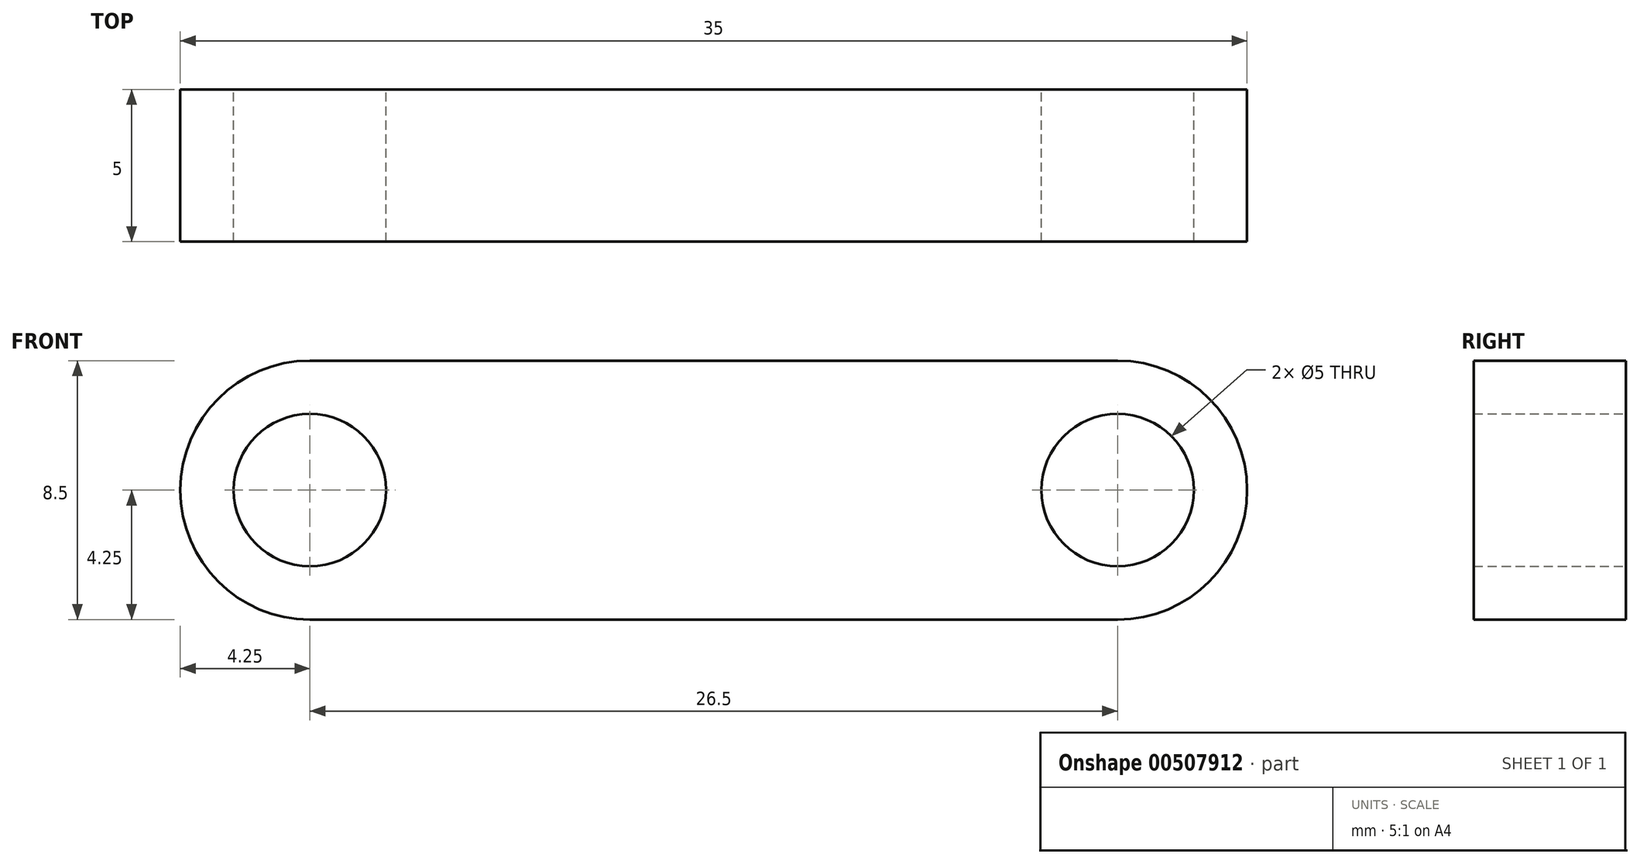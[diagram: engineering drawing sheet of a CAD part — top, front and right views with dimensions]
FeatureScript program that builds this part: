
annotation { "Feature Type Name" : "Feature", "Feature Type Description" : "" }
export const myFeature = defineFeature(function(context is Context, id is Id, definition is map)
    precondition{}
    {
        {
            var Q0;
            Q0=qCreatedBy(makeId("Front.planeOp"),FACE);
            var sketch = newSketch(context, id + "F0", { "sketchPlane" : qUnion([Q0])});
            skCircle(sketch, "E0", {"center": v(0, 0) * mm, "radius": 2.5 * mm});
            skLineSegment(sketch, "E1", {"start": v(0, 0) * mm, "end": v(26.5, 0) * mm, "construction": true});
            skCircle(sketch, "E2", {"center": v(26.5, 0) * mm, "radius": 2.5 * mm});
            skCircle(sketch, "E3", {"center": v(0, 0) * mm, "radius": 4.25 * mm});
            skCircle(sketch, "E4", {"center": v(26.5, 0) * mm, "radius": 4.25 * mm});
            skLineSegment(sketch, "E5", {"start": v(0, -4.25) * mm, "end": v(26.5, -4.25) * mm});
            skLineSegment(sketch, "E6", {"start": v(0, 4.25) * mm, "end": v(26.5, 4.25) * mm});
            skSolve(sketch);
        }
        {
            var Q0;
            Q0=makeQuery(id+"F0.imprint","IMPRINT",FACE,{"disambiguationData":[TD([[makeQuery(id+"F0.imprint","IMPRINT",EDGE,{"derivedFrom":sQuery(id+"F0.wireOp",EDGE,"E0")}),-1.0]])]});
            var Q1;
            Q1=makeQuery(id+"F0.imprint","IMPRINT",FACE,{"disambiguationData":[TD([[makeQuery(id+"F0.imprint","IMPRINT",EDGE,{"derivedFrom":sQuery(id+"F0.wireOp",EDGE,"E2")}),-1.0]])]});
            var Q2;
            {var subQ0=sQuery(id+"F0.wireOp",EDGE,"E5");Q2=makeQuery(id+"F0.imprint","IMPRINT",FACE,{"disambiguationData":[TD([[makeQuery(id+"F0.imprint","IMPRINT",EDGE,{"derivedFrom":subQ0}),1.0]])]});}
            var Q3;
            Q3=sQuery(id+"F0.wireOp",EDGE,"E0");
            var Q4;
            Q4=sQuery(id+"F0.wireOp",EDGE,"E3");
            var Q5;
            Q5=sQuery(id+"F0.wireOp",EDGE,"E6");
            var Q6;
            Q6=sQuery(id+"F0.wireOp",EDGE,"E5");
            var Q7;
            Q7=sQuery(id+"F0.wireOp",EDGE,"E4");
            var Q8;
            Q8=sQuery(id+"F0.wireOp",EDGE,"E2");
            extrude(context, id + "F1", {"entities" : qUnion([Q0, Q1, Q2]), "surfaceEntities" : qUnion([Q3, Q4, Q5, Q6, Q7, Q8]), "depth" : 5 * mm, "offsetDistance" : 25 * mm});
        }
    });
